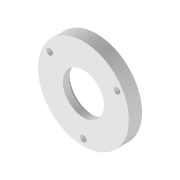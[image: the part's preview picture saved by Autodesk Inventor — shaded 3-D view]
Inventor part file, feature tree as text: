
AUTODESK INVENTOR PART (.ipt)
format: ipt  version: 2022 (Build 260153000, 153)  size: 123,904 bytes
history: native  units: mm
features: reference x7, other x4, sketch x2, revolve x1, extrude x1
ambient origin geometry x8: Origin, YZ Plane, XZ Plane, XY Plane, X Axis, Y Axis, Z Axis, Center Point
bodies: Volumenkörper1 (feature_tree)
feature tree (15):
  revolve  "Umdrehung1"
  extrude  "Extrusion1"  Depth=2.5mm
  sketch  "Skizze1"  dims[d0=2.5mm d1=2.5mm]
  reference  "Referenz1"
  reference  "Referenz2"
  reference  "Referenz3"
  sketch  "Skizze2"  dims[d3=16.097056mm d4=8.048528mm d5=11.25mm d6=90.0deg d7=10.0mm d8=0.0mm]
  reference  "Referenz4"
  reference  "Referenz5"
  reference  "Referenz6"
  reference  "Referenz7"
  other  "Assembly_ETL_v0.iam"
  other  "50_ETL_Lid_v0:1"
  other  "50_ETL_Membrane_v0:1"
  other  "50_ETL_28by_coil:1"
